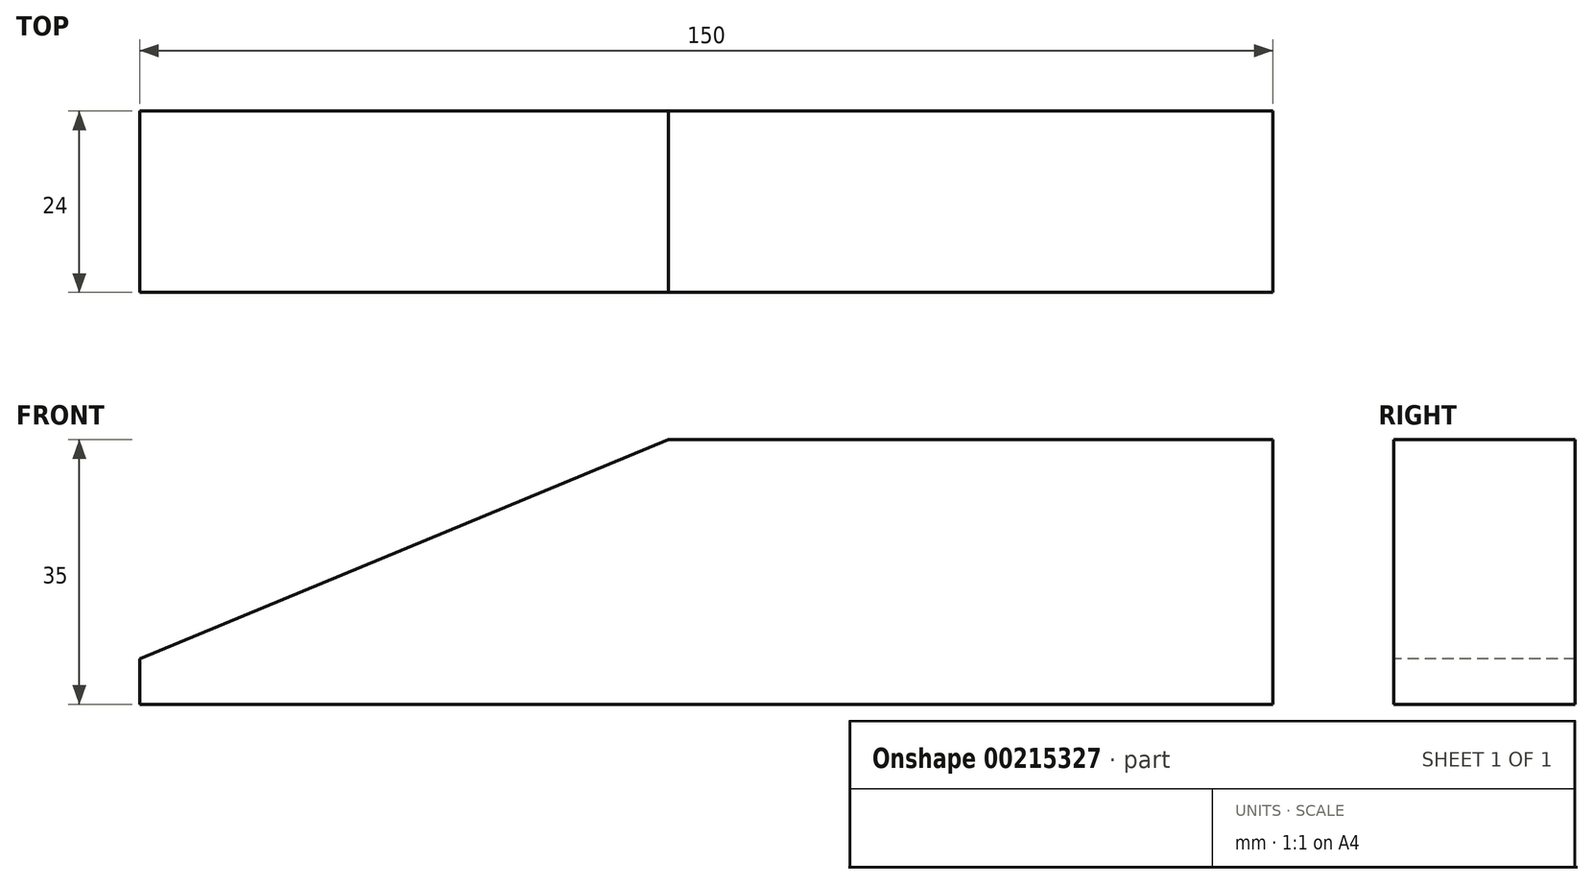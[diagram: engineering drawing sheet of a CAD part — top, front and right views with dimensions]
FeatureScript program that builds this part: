
annotation { "Feature Type Name" : "Feature", "Feature Type Description" : "" }
export const myFeature = defineFeature(function(context is Context, id is Id, definition is map)
    precondition{}
    {
        {
            var Q0;
            Q0=qCreatedBy(makeId("Front.planeOp"),FACE);
            var sketch = newSketch(context, id + "F0", { "sketchPlane" : qUnion([Q0])});
            skLineSegment(sketch, "E0.bottom", {"start": v(-75, 17.5) * mm, "end": v(75, 17.5) * mm});
            skLineSegment(sketch, "E0.top", {"start": v(-75, -17.5) * mm, "end": v(75, -17.5) * mm});
            skLineSegment(sketch, "E0.left", {"start": v(-75, 17.5) * mm, "end": v(-75, -17.5) * mm});
            skLineSegment(sketch, "E0.right", {"start": v(75, 17.5) * mm, "end": v(75, -17.5) * mm});
            skPoint(sketch, "E0.middle", {"position": v(0, 0) * mm});
            skLineSegment(sketch, "E1", {"start": v(75, 17.5) * mm, "end": v(75, -11.82) * mm});
            skSolve(sketch);
        }
        {
            var Q0;
            Q0 = qSketchRegion(id + "F0", true);
            extrude(context, id + "F1", {"entities" : qUnion([Q0]), "depth" : 24 * mm});
        }
        {
            var Q0;
            Q0=makeQuery(id+"F1.opExtrude","CAP_FACE",FACE,{"disambiguationData":[OSD([sQuery(id+"F0.wireOp",EDGE,"E0.bottom"),sQuery(id+"F0.wireOp",EDGE,"E0.top"),sQuery(id+"F0.wireOp",EDGE,"E0.left"),sQuery(id+"F0.wireOp",EDGE,"E0.right"),sQuery(id+"F0.wireOp",EDGE,"E1")])],"isStart":false});
            var sketch = newSketch(context, id + "F2", { "sketchPlane" : qUnion([Q0])});
            skLineSegment(sketch, "E2", {"start": v(-75, 17.5) * mm, "end": v(-75, -11.5) * mm});
            skLineSegment(sketch, "E3", {"start": v(-75, 17.5) * mm, "end": v(-5, 17.5) * mm});
            skLineSegment(sketch, "E4", {"start": v(-75, -11.5) * mm, "end": v(-5, 17.5) * mm});
            skSolve(sketch);
        }
        {
            var Q0;
            Q0 = qSketchRegion(id + "F2", true);
            extrude(context, id + "F3", {"entities" : qUnion([Q0]), "operationType" : NewBodyOperationType.REMOVE, "oppositeDirection" : true, "depth" : 25 * mm});
        }
    });
